annotation { "Feature Type Name" : "Feature", "Feature Type Description" : "" }
export const myFeature = defineFeature(function(context is Context, id is Id, definition is map)
    precondition{}
    {
        {
            var Q0;
            Q0=qCreatedBy(makeId("Front.planeOp"),FACE);
            var sketch = newSketch(context, id + "F0", { "sketchPlane" : qUnion([Q0])});
            skLineSegment(sketch, "E0", {"start": v(-32.58, 52.68) * mm, "end": v(-32.58, -61.62) * mm});
            skLineSegment(sketch, "E1", {"start": v(-32.58, -61.62) * mm, "end": v(11.87, -61.62) * mm});
            skCircle(sketch, "E2", {"center": v(-32.58, 52.68) * mm, "radius": 9.53 * mm});
            skCircle(sketch, "E3", {"center": v(-32.58, 24.15) * mm, "radius": 15.88 * mm});
            skCircle(sketch, "E4", {"center": v(-32.58, -61.62) * mm, "radius": 9.53 * mm});
            skCircle(sketch, "E5", {"center": v(11.87, -61.62) * mm, "radius": 7.94 * mm});
            skCircle(sketch, "E6", {"center": v(-32.58, 24.15) * mm, "radius": 3.5 * mm});
            skCircle(sketch, "E7", {"center": v(-32.58, -61.62) * mm, "radius": 3.1 * mm});
            skCircle(sketch, "E8", {"center": v(-32.58, 52.68) * mm, "radius": 4.92 * mm});
            skLineSegment(sketch, "E9", {"start": v(-23.2, 51.03) * mm, "end": v(-16.7, 24.05) * mm});
            skLineSegment(sketch, "E10", {"start": v(-16.7, 24.05) * mm, "end": v(-19.95, -47.46) * mm});
            skPoint(sketch, "E10.endSnap0", {"position": v(-19.95, 37.54) * mm});
            skLineSegment(sketch, "E11", {"start": v(-42.06, 51.82) * mm, "end": v(-47.99, 27.98) * mm});
            skLineSegment(sketch, "E12", {"start": v(-47.99, 27.98) * mm, "end": v(-42.08, -62.24) * mm});
            skLineSegment(sketch, "E13", {"start": v(-19.95, -47.46) * mm, "end": v(-22.86, -61.62) * mm});
            skLineSegment(sketch, "E14", {"start": v(-29.05, -52.77) * mm, "end": v(14.59, -54.16) * mm});
            skLineSegment(sketch, "E15", {"start": v(-34.26, -71) * mm, "end": v(11.87, -69.56) * mm});
            skText(sketch, "E16", { "text": "Kayla Stumpf", "fontName": "OpenSans-Regular.ttf"});
            const initialGuessF0  = {"E16": [0.0157, 0.0083, 1, 0, 0.01426]};
            skSetInitialGuess(sketch, initialGuessF0);
            skSolve(sketch);
        }
        {
            var Q0;
            Q0 = qSketchRegion(id + "F0", true);
            extrude(context, id + "F1", {"entities" : qUnion([Q0]), "depth" : 25.4 * mm, "offsetDistance" : 25.4 * mm});
        }
    });